# Revit family: TapSet_Wall_Nero_Mecca_BasinBath_220
name_source: partatom
category: Plumbing Fixtures
units: mm (PartAtom-declared; Revit-internal decimal feet)

## family parameters
Always vertical = Yes
Cut with Voids When Loaded = Yes
Maintain Annotation Orientation = No
OmniClass Number = 23.31.11.19
OmniClass Title = Faucet Mixing Valves
Part Type = Normal
Room Calculation Point = No
Round Connector Dimension = Use Diameter
Shared = No
Work Plane-Based = No

## types (7) — shared parameters
Assembly Code = D2010
CW Connection = Yes
Default Elevation = 1050 mm
HW Connection = Yes
IfcExportAs = IfcValve
IfcExportType = MIXING
Manufacturer = Nero
ManufacturerOverallDepth = 230 mm
ManufacturerOverallHeight = 65 mm
ManufacturerOverallWidth = 340 mm
ModifiedIssue = 20251009 $
URL = https://nerotapware.com.au
Uniclass2015Code = Pr_40_20_87
Uniclass2015Title = Taps and water supply outlet fittings
Uniclass2015Version = Products v1.35
Vent Connection = No
Waste Connection = No
zero-valued in all types: CWFU, HWFU, WFU

## per-type parameters (varying)
| type | Description | ManufacturerSpecCode | Material | Model | Type Comments |
| Chrome (25D008CH) | Mecca Wall Basin/Bath Set 220mm Spout Chrome | 25D008CH | Metal_Chrome_Nero | 25D008CH | Tap Set - Wall - Basin Bath - 220 - Chrome |
| Matte Black (25D008MB) | Mecca Wall Basin/Bath Set 220mm Spout Matte Black | 25D008MB | Metal_MatteBlack_Nero | 25D008MB | Tap Set - Wall - Basin Bath - 220 - Matte Black |
| Brushed Nickel (25D008BN) | Mecca Wall Basin/Bath Set 220mm Spout Brushed Nickel | 25D008BN | Metal_Nickel_Nero_Brushed | 25D008BN | Tap Set - Wall - Basin Bath - 220 - Brushed Nickel |
| Gun Metal (25D008GM) | Mecca Wall Basin/Bath Set 220mm Spout Gun Metal | 25D008GM | Metal_GunMetal_Nero | 25D008GM | Tap Set - Wall - Basin Bath - 220 - Gun Metal |
| Brushed Gold (25D008BG) | Mecca Wall Basin/Bath Set 220mm Spout Brushed Gold | 25D008BG | Metal_Gold_Nero_Brushed | 25D008BG | Tap Set - Wall - Basin Bath - 220 - Brushed Gold |
| Brushed Bronze (25D008BZ) | Mecca Wall Basin/Bath Set 220mm Spout Brushed Bronze | 25D008BZ | Metal_Bronze_Nero_Brushed | 25D008BZ | Tap Set - Wall - Basin Bath - 220 - Brushed Bronze |
| Matte White (25D008MW) | Mecca Wall Basin/Bath Set 220mm Spout Matte White | 25D008MW | Metal_MatteWhite_Nero | 25D008MW | Tap Set - Wall - Basin Bath - 220 - Matte White |

## geometry (parser evidence)
native form markers: Sweep x1
no freeform markers — native parametric forms only
